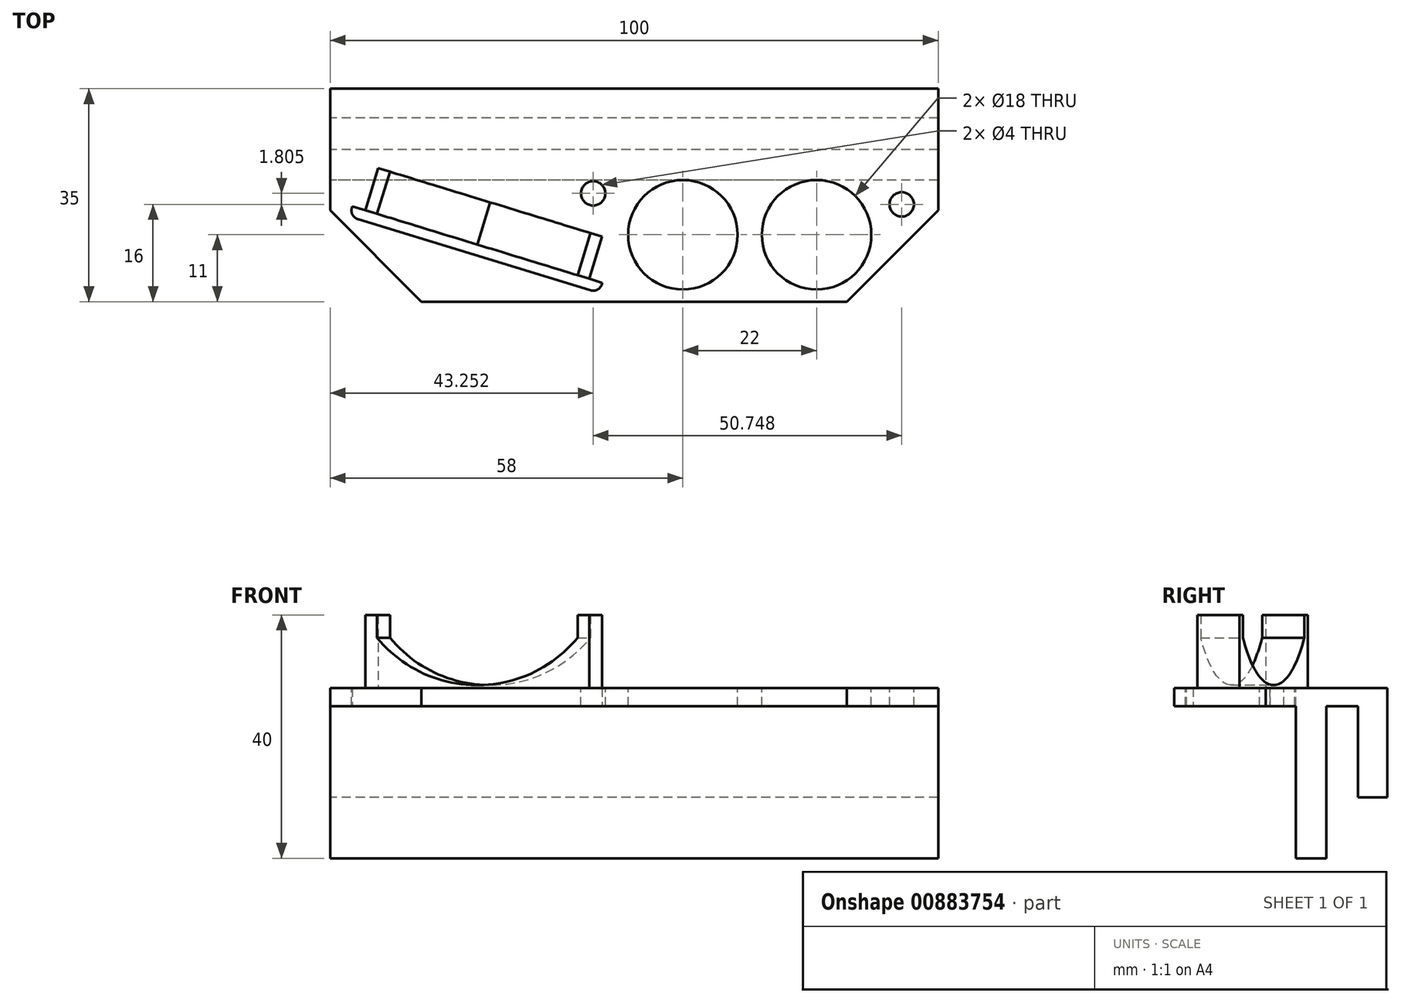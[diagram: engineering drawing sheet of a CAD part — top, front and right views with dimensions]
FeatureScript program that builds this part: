
annotation { "Feature Type Name" : "Feature", "Feature Type Description" : "" }
export const myFeature = defineFeature(function(context is Context, id is Id, definition is map)
    precondition{}
    {
        {
            var Q0;
            Q0=qCreatedBy(makeId("Top.planeOp"),FACE);
            var sketch = newSketch(context, id + "F0", { "sketchPlane" : qUnion([Q0])});
            skLineSegment(sketch, "E0.bottom", {"start": v(50, -17.5) * mm, "end": v(-50, -17.5) * mm});
            skLineSegment(sketch, "E0.top", {"start": v(50, 17.5) * mm, "end": v(-50, 17.5) * mm});
            skLineSegment(sketch, "E0.left", {"start": v(50, -17.5) * mm, "end": v(50, 17.5) * mm});
            skLineSegment(sketch, "E0.right", {"start": v(-50, -17.5) * mm, "end": v(-50, 17.5) * mm});
            skPoint(sketch, "E0.middle", {"position": v(0, 0) * mm});
            skSolve(sketch);
        }
        {
            var Q0;
            Q0=makeQuery(id+"F0.imprint","IMPRINT",FACE,{"disambiguationData":[TD([[makeQuery(id+"F0.imprint","IMPRINT",EDGE,{"derivedFrom":sQuery(id+"F0.wireOp",EDGE,"E0.bottom")}),-1.0]])]});
            extrude(context, id + "F1", {"entities" : qUnion([Q0]), "oppositeDirection" : true, "depth" : 3 * mm, "offsetDistance" : 25 * mm});
        }
        {
            var Q0;
            Q0=makeQuery(id+"F1.opExtrude","CAP_FACE",FACE,{"disambiguationData":[OSD([sQuery(id+"F0.wireOp",EDGE,"E0.bottom"),sQuery(id+"F0.wireOp",EDGE,"E0.top"),sQuery(id+"F0.wireOp",EDGE,"E0.left"),sQuery(id+"F0.wireOp",EDGE,"E0.right")])],"isStart":false});
            var sketch = newSketch(context, id + "F2", { "sketchPlane" : qUnion([Q0])});
            skLineSegment(sketch, "E1.bottom", {"start": v(50, -17.5) * mm, "end": v(-50, -17.5) * mm});
            skLineSegment(sketch, "E1.top", {"start": v(50, -12.7) * mm, "end": v(-50, -12.7) * mm});
            skLineSegment(sketch, "E1.left", {"start": v(50, -17.5) * mm, "end": v(50, -12.7) * mm});
            skLineSegment(sketch, "E1.right", {"start": v(-50, -17.5) * mm, "end": v(-50, -12.7) * mm});
            skLineSegment(sketch, "E2.bottom", {"start": v(50, 17.5) * mm, "end": v(-50, 17.5) * mm});
            skLineSegment(sketch, "E2.top", {"start": v(50, -7.5) * mm, "end": v(-50, -7.5) * mm});
            skLineSegment(sketch, "E2.left", {"start": v(50, 17.5) * mm, "end": v(50, -7.5) * mm});
            skLineSegment(sketch, "E2.right", {"start": v(-50, 17.5) * mm, "end": v(-50, -7.5) * mm});
            skLineSegment(sketch, "E3", {"start": v(50, -7.5) * mm, "end": v(50, -2.5) * mm});
            skLineSegment(sketch, "E4", {"start": v(50, -2.5) * mm, "end": v(-50, -2.5) * mm});
            skSolve(sketch);
        }
        {
            var Q0;
            {var subQ0=sQuery(id+"F2.wireOp",EDGE,"E2.top");Q0=makeQuery(id+"F2.imprint","IMPRINT",FACE,{"disambiguationData":[TD([[makeQuery(id+"F2.imprint","IMPRINT",EDGE,{"derivedFrom":subQ0}),-1.0]])]});}
            extrude(context, id + "F3", {"entities" : qUnion([Q0]), "operationType" : NewBodyOperationType.ADD, "depth" : 25 * mm, "offsetDistance" : 25 * mm});
        }
        {
            var Q0;
            Q0=makeQuery(id+"F2.imprint","IMPRINT",FACE,{"disambiguationData":[TD([[makeQuery(id+"F2.imprint","IMPRINT",EDGE,{"derivedFrom":sQuery(id+"F2.wireOp",EDGE,"E1.bottom")}),-1.0]])]});
            extrude(context, id + "F4", {"entities" : qUnion([Q0]), "operationType" : NewBodyOperationType.ADD, "depth" : 15 * mm, "offsetDistance" : 25 * mm});
        }
        {
            var Q0;
            Q0=makeQuery(id+"F1.opExtrude","SWEPT_EDGE",EDGE,{"disambiguationData":[OSD([sQuery(id+"F0.wireOp",EDGE,"E0.bottom"),sQuery(id+"F0.wireOp",EDGE,"E0.left")])]});
            var Q1;
            Q1=makeQuery(id+"F1.opExtrude","SWEPT_EDGE",EDGE,{"disambiguationData":[OSD([sQuery(id+"F0.wireOp",EDGE,"E0.bottom"),sQuery(id+"F0.wireOp",EDGE,"E0.right")])]});
            chamfer(context, id + "F5", {"entities" : qUnion([Q0, Q1]), "width" : 15 * mm, "tangentPropagation" : true});
        }
        {
            var Q0;
            Q0=makeQuery(id+"F1.opExtrude","CAP_FACE",FACE,{"disambiguationData":[OSD([sQuery(id+"F0.wireOp",EDGE,"E0.bottom"),sQuery(id+"F0.wireOp",EDGE,"E0.top"),sQuery(id+"F0.wireOp",EDGE,"E0.left"),sQuery(id+"F0.wireOp",EDGE,"E0.right")])],"isStart":true});
            var sketch = newSketch(context, id + "F6", { "sketchPlane" : qUnion([Q0])});
            skLineSegment(sketch, "E5.0", {"start": v(50, 7.5) * mm, "end": v(-50, 7.5) * mm, "construction": true});
            skLineSegment(sketch, "E6", {"start": v(-45, -2.5) * mm, "end": v(-6.75, -14.2) * mm, "construction": true});
            skArc(sketch, "E7", {"start": v(-7.19, -15.63) * mm, "mid": v(-5.31, -14.63) * mm, "end": v(-6.3, -12.76) * mm});
            skArc(sketch, "E8", {"start": v(-44.56, -1.07) * mm, "mid": v(-46.43, -2.06) * mm, "end": v(-45.44, -3.93) * mm});
            skLineSegment(sketch, "E9", {"start": v(-45, -2.5) * mm, "end": v(-45.44, -3.93) * mm, "construction": true});
            skLineSegment(sketch, "E10", {"start": v(-45.44, -3.93) * mm, "end": v(-7.19, -15.63) * mm});
            skLineSegment(sketch, "E11", {"start": v(-6.75, -14.2) * mm, "end": v(-6.3, -12.76) * mm});
            skLineSegment(sketch, "E12", {"start": v(-6.3, -12.76) * mm, "end": v(-44.56, -1.07) * mm});
            skCircle(sketch, "E13", {"center": v(30, -6.5) * mm, "radius": 9 * mm});
            skCircle(sketch, "E14", {"center": v(8, -6.5) * mm, "radius": 9 * mm});
            skLineSegment(sketch, "E15", {"start": v(30, -6.5) * mm, "end": v(8, -6.5) * mm, "construction": true});
            skLineSegment(sketch, "E16", {"start": v(30, -6.5) * mm, "end": v(30, 2.5) * mm, "construction": true});
            skPoint(sketch, "E17.centerSnap0", {"position": v(19, -6.5) * mm});
            skCircle(sketch, "E18", {"center": v(-6.75, 0.3) * mm, "radius": 2 * mm});
            skLineSegment(sketch, "E19", {"start": v(-6.75, -14.2) * mm, "end": v(-6.75, 0.3) * mm, "construction": true});
            skCircle(sketch, "E20", {"center": v(44, -1.5) * mm, "radius": 2 * mm});
            skCircle(sketch, "E21", {"center": v(-6.75, 0.3) * mm, "radius": 5.5 * mm, "construction": true});
            skLineSegment(sketch, "E22", {"start": v(-11.07, -12.87) * mm, "end": v(-8.44, -4.27) * mm});
            skSolve(sketch);
        }
        {
            var Q0;
            Q0 = qSketchRegion(id + "F6", true);
            extrude(context, id + "F7", {"entities" : qUnion([Q0]), "operationType" : NewBodyOperationType.REMOVE, "oppositeDirection" : true, "depth" : 30 * mm, "offsetDistance" : 25 * mm});
        }
        {
            var Q0;
            Q0=makeQuery(id+"F7.boolean.opBoolean","COPY",FACE,{"derivedFrom":makeQuery(id+"F7.opExtrude","SWEPT_FACE",FACE,{"disambiguationData":[OSD([sQuery(id+"F6.wireOp",EDGE,"E12")])]})});
            var sketch = newSketch(context, id + "F8", { "sketchPlane" : qUnion([Q0])});
            skLineSegment(sketch, "E23", {"start": v(-22.3, 0) * mm, "end": v(-39.55, 0) * mm});
            skLineSegment(sketch, "E24", {"start": v(-39.55, 0) * mm, "end": v(-39.55, 8.25) * mm});
            skLineSegment(sketch, "E25", {"start": v(-22.3, 0) * mm, "end": v(-5.05, 0) * mm});
            skLineSegment(sketch, "E26", {"start": v(-5.05, 0) * mm, "end": v(-5.05, 8.25) * mm});
            skArc(sketch, "E27", {"start": v(-22.3, 0.5) * mm, "mid": v(-12.82, 2.48) * mm, "end": v(-5.05, 8.25) * mm});
            skLineSegment(sketch, "E28", {"start": v(-22.3, 0) * mm, "end": v(-22.3, 0.5) * mm, "construction": true});
            skArc(sketch, "E29.MirrorCS", {"start": v(-22.3, 0.5) * mm, "mid": v(-31.78, 2.48) * mm, "end": v(-39.55, 8.25) * mm});
            skLineSegment(sketch, "E30.bottom", {"start": v(-39.55, 0) * mm, "end": v(-5.05, 0) * mm});
            skLineSegment(sketch, "E30.top", {"start": v(-39.55, -3) * mm, "end": v(-5.05, -3) * mm});
            skLineSegment(sketch, "E30.left", {"start": v(-39.55, 0) * mm, "end": v(-39.55, -3) * mm});
            skLineSegment(sketch, "E30.right", {"start": v(-5.05, 0) * mm, "end": v(-5.05, -3) * mm});
            skSolve(sketch);
        }
        {
            var Q0;
            Q0 = qSketchRegion(id + "F8", true);
            extrude(context, id + "F9", {"entities" : qUnion([Q0]), "depth" : 1.25 * mm, "offsetDistance" : 25 * mm});
        }
        {
            var Q0;
            Q0=makeQuery(id+"F8.imprint","IMPRINT",FACE,{"disambiguationData":[TD([[makeQuery(id+"F8.imprint","IMPRINT",EDGE,{"derivedFrom":sQuery(id+"F8.wireOp",EDGE,"E24")}),-1.0]])]});
            extrude(context, id + "F10", {"entities" : qUnion([Q0]), "operationType" : NewBodyOperationType.ADD, "oppositeDirection" : true, "depth" : 6 * mm, "offsetDistance" : 25 * mm});
        }
        {
            var Q0;
            Q0=makeQuery(id+"F9.opExtrude","SWEPT_FACE",FACE,{"disambiguationData":[OSD([sQuery(id+"F8.wireOp",EDGE,"E30.top")])]});
            var sketch = newSketch(context, id + "F11", { "sketchPlane" : qUnion([Q0])});
            skArc(sketch, "E31.0", {"start": v(-44.56, 1.07) * mm, "mid": v(-45.6, 1.12) * mm, "end": v(-46.34, 1.83) * mm});
            skLineSegment(sketch, "E32", {"start": v(-42.3, 3.06) * mm, "end": v(-46.34, 1.83) * mm});
            skPoint(sketch, "E33.orphan", {"position": v(-45.44, 3.93) * mm});
            skLineSegment(sketch, "E34.0", {"start": v(-42.3, 3.06) * mm, "end": v(-41.93, 1.87) * mm});
            skLineSegment(sketch, "E35", {"start": v(-25.44, 6.91) * mm, "end": v(-25.8, 8.1) * mm, "construction": true});
            skLineSegment(sketch, "E36.trimOffspring", {"start": v(-41.93, 1.87) * mm, "end": v(-44.56, 1.07) * mm});
            skPoint(sketch, "E37.0.start.orphan", {"position": v(-6.3, 12.76) * mm});
            skLineSegment(sketch, "E38.MirrorCS", {"start": v(-9.3, 13.15) * mm, "end": v(-8.94, 11.96) * mm});
            skLineSegment(sketch, "E39.MirrorCS", {"start": v(-9.3, 13.15) * mm, "end": v(-5.26, 14.39) * mm});
            skLineSegment(sketch, "E40.MirrorCS", {"start": v(-8.94, 11.96) * mm, "end": v(-6.3, 12.76) * mm});
            skArc(sketch, "E41.MirrorCS", {"start": v(-6.3, 12.76) * mm, "mid": v(-5.49, 13.38) * mm, "end": v(-5.26, 14.39) * mm});
            skPoint(sketch, "E42.MirrorP", {"position": v(-7.19, 15.63) * mm});
            skSolve(sketch);
        }
        {
            var Q0;
            Q0=makeQuery(id+"F11.imprint","IMPRINT",FACE,{"disambiguationData":[TD([[makeQuery(id+"F11.imprint","IMPRINT",EDGE,{"derivedFrom":sQuery(id+"F11.wireOp",EDGE,"E31.0")}),-1.0]])]});
            var Q1;
            Q1=makeQuery(id+"F11.imprint","IMPRINT",FACE,{"disambiguationData":[TD([[makeQuery(id+"F11.imprint","IMPRINT",EDGE,{"derivedFrom":sQuery(id+"F11.wireOp",EDGE,"E38.MirrorCS")}),1.0]])]});
            var Q2;
            Q2=makeQuery(id+"F1.opExtrude","CAP_FACE",FACE,{"disambiguationData":[OSD([sQuery(id+"F0.wireOp",EDGE,"E0.bottom"),sQuery(id+"F0.wireOp",EDGE,"E0.top"),sQuery(id+"F0.wireOp",EDGE,"E0.left"),sQuery(id+"F0.wireOp",EDGE,"E0.right")])],"isStart":true});
            var Q3;
            Q3=makeQuery(id+"F9.opExtrude","CAP_VERTEX",VERTEX,{"disambiguationData":[OSD([sQuery(id+"F8.wireOp",EDGE,"E26"),sQuery(id+"F8.wireOp",EDGE,"E27")])],"isStart":false});
            extrude(context, id + "F12", {"entities" : qUnion([Q0, Q1]), "operationType" : NewBodyOperationType.ADD, "endBound" : BoundingType.UP_TO_SURFACE, "oppositeDirection" : true, "depth" : 25 * mm, "endBoundEntityFace" : qUnion([Q2]), "endBoundEntityVertex" : qUnion([Q3]), "offsetDistance" : 25 * mm});
        }
        {
            var Q0;
            Q0=makeQuery(id+"F12.opExtrude","CAP_FACE",FACE,{"disambiguationData":[OSD([sQuery(id+"F11.wireOp",EDGE,"E38.MirrorCS"),sQuery(id+"F11.wireOp",EDGE,"E39.MirrorCS"),sQuery(id+"F11.wireOp",EDGE,"E40.MirrorCS"),sQuery(id+"F11.wireOp",EDGE,"E41.MirrorCS")])],"isStart":false});
            var sketch = newSketch(context, id + "F13", { "sketchPlane" : qUnion([Q0])});
            skLineSegment(sketch, "E43", {"start": v(-9.3, -13.15) * mm, "end": v(-7.18, -6.22) * mm});
            skLineSegment(sketch, "E44", {"start": v(-7.18, -6.22) * mm, "end": v(-5.27, -6.8) * mm});
            skLineSegment(sketch, "E45", {"start": v(-5.27, -6.8) * mm, "end": v(-7.4, -13.74) * mm});
            skLineSegment(sketch, "E46", {"start": v(-9.3, -13.15) * mm, "end": v(-7.4, -13.74) * mm});
            skLineSegment(sketch, "E47", {"start": v(-42.3, -3.06) * mm, "end": v(-9.3, -13.15) * mm, "construction": true});
            skLineSegment(sketch, "E48", {"start": v(-25.8, -8.1) * mm, "end": v(-25.14, -5.94) * mm, "construction": true});
            skLineSegment(sketch, "E49.MirrorCS", {"start": v(-42.3, -3.06) * mm, "end": v(-44.2, -2.48) * mm});
            skLineSegment(sketch, "E50.MirrorCS", {"start": v(-42.3, -3.06) * mm, "end": v(-40.18, 3.87) * mm});
            skLineSegment(sketch, "E51.MirrorCS", {"start": v(-40.18, 3.87) * mm, "end": v(-42.09, 4.45) * mm});
            skLineSegment(sketch, "E52.MirrorCS", {"start": v(-42.09, 4.45) * mm, "end": v(-44.2, -2.48) * mm});
            skSolve(sketch);
        }
        {
            var Q0;
            Q0 = qSketchRegion(id + "F13", true);
            extrude(context, id + "F14", {"entities" : qUnion([Q0]), "operationType" : NewBodyOperationType.ADD, "depth" : 12 * mm, "offsetDistance" : 25 * mm});
        }
    });
